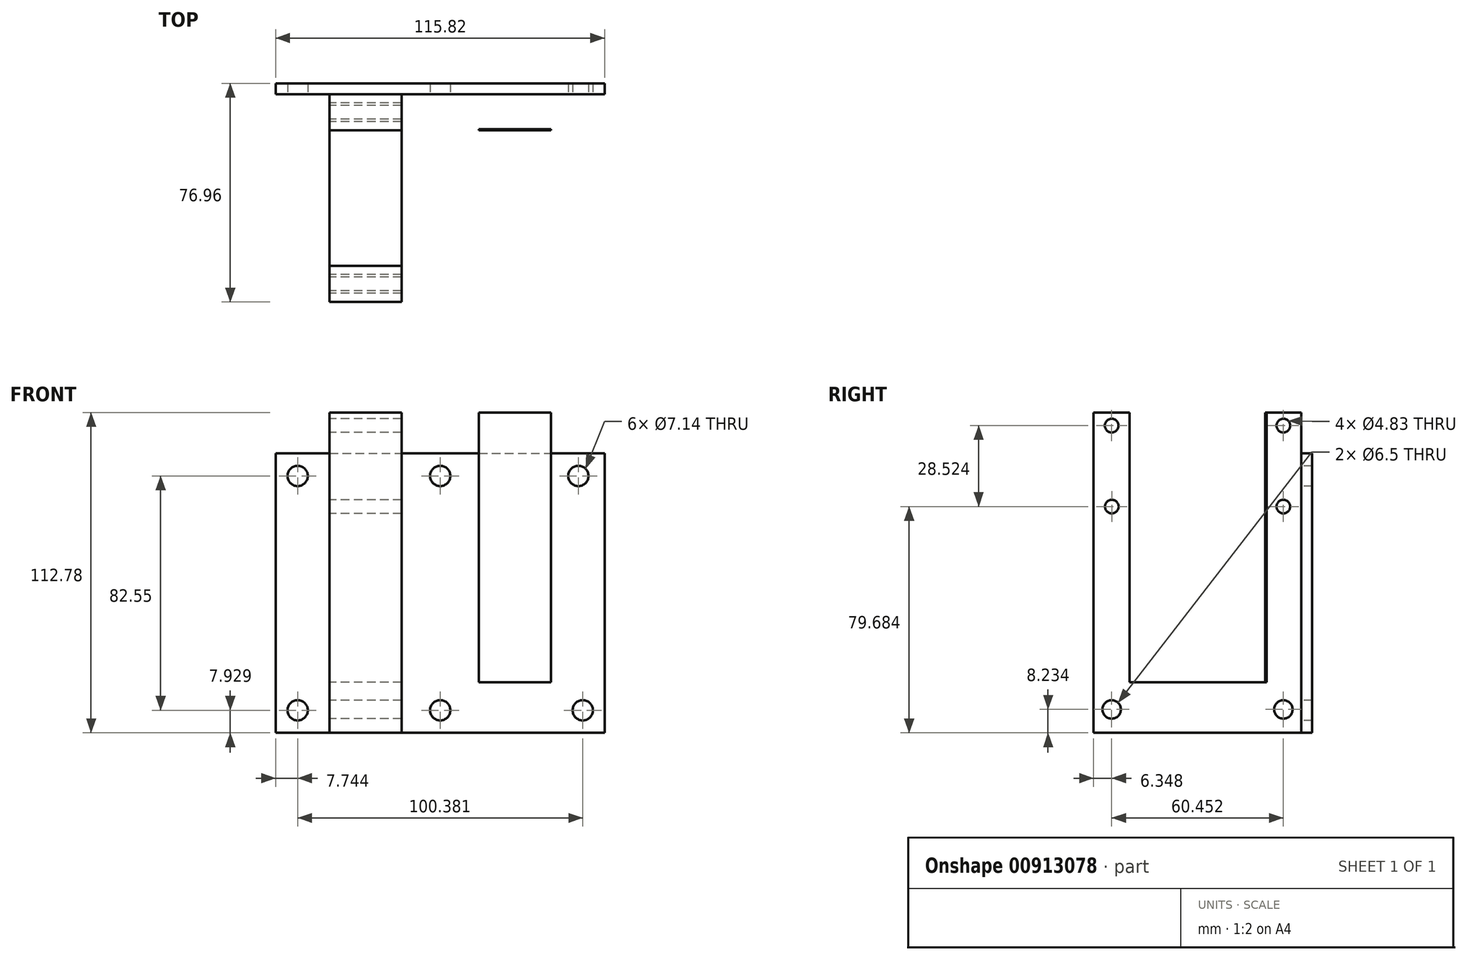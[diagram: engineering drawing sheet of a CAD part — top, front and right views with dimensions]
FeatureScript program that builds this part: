
annotation { "Feature Type Name" : "Feature", "Feature Type Description" : "" }
export const myFeature = defineFeature(function(context is Context, id is Id, definition is map)
    precondition{}
    {
        {
            var Q0;
            Q0=qCreatedBy(makeId("Front.planeOp"),FACE);
            var sketch = newSketch(context, id + "F0", { "sketchPlane" : qUnion([Q0])});
            skLineSegment(sketch, "E0", {"start": v(-55.41, 38.66) * mm, "end": v(60.41, 38.66) * mm});
            skLineSegment(sketch, "E1", {"start": v(60.41, 38.66) * mm, "end": v(60.41, -59.74) * mm});
            skLineSegment(sketch, "E2", {"start": v(60.41, -59.74) * mm, "end": v(-55.41, -59.74) * mm});
            skLineSegment(sketch, "E3", {"start": v(-55.41, 38.66) * mm, "end": v(-55.41, -59.74) * mm});
            skCircle(sketch, "E4", {"center": v(-47.67, -51.81) * mm, "radius": 3.57 * mm});
            skCircle(sketch, "E5", {"center": v(2.52, -51.81) * mm, "radius": 3.57 * mm});
            skCircle(sketch, "E6", {"center": v(52.71, -51.81) * mm, "radius": 3.57 * mm});
            skCircle(sketch, "E7", {"center": v(-47.67, 30.74) * mm, "radius": 3.57 * mm});
            skCircle(sketch, "E8", {"center": v(2.52, 30.74) * mm, "radius": 3.57 * mm});
            skCircle(sketch, "E9", {"center": v(51.17, 30.74) * mm, "radius": 3.57 * mm});
            skLineSegment(sketch, "E10.bottom", {"start": v(-36.46, -59.74) * mm, "end": v(-11.06, -59.74) * mm});
            skLineSegment(sketch, "E10.top", {"start": v(-36.46, 53.04) * mm, "end": v(-11.06, 53.04) * mm});
            skLineSegment(sketch, "E10.left", {"start": v(-36.46, -59.74) * mm, "end": v(-36.46, 53.04) * mm});
            skLineSegment(sketch, "E10.right", {"start": v(-11.06, -59.74) * mm, "end": v(-11.06, 53.04) * mm});
            skLineSegment(sketch, "E11.bottom", {"start": v(16.11, -59.74) * mm, "end": v(41.51, -59.74) * mm});
            skLineSegment(sketch, "E11.top", {"start": v(16.11, 53.04) * mm, "end": v(41.51, 53.04) * mm});
            skLineSegment(sketch, "E11.left", {"start": v(16.11, -59.74) * mm, "end": v(16.11, 53.04) * mm});
            skLineSegment(sketch, "E11.right", {"start": v(41.51, -59.74) * mm, "end": v(41.51, 53.04) * mm});
            skSolve(sketch);
        }
        {
            var Q0;
            {var subQ5=sQuery(id+"F0.wireOp",EDGE,"E10.top");Q0=makeQuery(id+"F0.imprint","IMPRINT",FACE,{"disambiguationData":[TD([[makeQuery(id+"F0.imprint","IMPRINT",EDGE,{"derivedFrom":subQ5}),-1.0]])]});}
            var Q1;
            {var subQ0=sQuery(id+"F0.wireOp",EDGE,"E10.right");var subQ1=sQuery(id+"F0.wireOp",EDGE,"E0");var subQ2=makeQuery(id+"F0.imprint","INTERSECT",VERTEX,{"derivedFrom":[subQ1,subQ0]});Q1=makeQuery(id+"F0.imprint","IMPRINT",FACE,{"disambiguationData":[TD([[makeQuery(id+"F0.imprint","IMPRINT",EDGE,{"disambiguationData":[TD([[subQ2,1.0]])],"derivedFrom":subQ1}),-1.0]])]});}
            var Q2;
            {var subQ0=sQuery(id+"F0.wireOp",EDGE,"E11.left");var subQ1=sQuery(id+"F0.wireOp",EDGE,"E0");var subQ2=makeQuery(id+"F0.imprint","INTERSECT",VERTEX,{"derivedFrom":[subQ1,subQ0]});Q2=makeQuery(id+"F0.imprint","IMPRINT",FACE,{"disambiguationData":[TD([[makeQuery(id+"F0.imprint","IMPRINT",EDGE,{"disambiguationData":[TD([[subQ2,-1.0]])],"derivedFrom":subQ1}),-1.0]])]});}
            var Q3;
            {var subQ5=sQuery(id+"F0.wireOp",EDGE,"E11.top");Q3=makeQuery(id+"F0.imprint","IMPRINT",FACE,{"disambiguationData":[TD([[makeQuery(id+"F0.imprint","IMPRINT",EDGE,{"derivedFrom":subQ5}),-1.0]])]});}
            extrude(context, id + "F1", {"entities" : qUnion([Q0, Q1, Q2, Q3]), "depth" : 73.15 * mm, "offsetDistance" : 25.4 * mm});
        }
        {
            var Q0;
            Q0=makeQuery(id+"F0.imprint","IMPRINT",FACE,{"disambiguationData":[TD([[makeQuery(id+"F0.imprint","IMPRINT",EDGE,{"derivedFrom":sQuery(id+"F0.wireOp",EDGE,"E5")}),-1.0]])]});
            var Q1;
            {var subQ1=sQuery(id+"F0.wireOp",EDGE,"E1");Q1=makeQuery(id+"F0.imprint","IMPRINT",FACE,{"disambiguationData":[TD([[makeQuery(id+"F0.imprint","IMPRINT",EDGE,{"derivedFrom":subQ1}),-1.0]])]});}
            var Q2;
            {var subQ0=sQuery(id+"F0.wireOp",EDGE,"E11.left");var subQ1=sQuery(id+"F0.wireOp",EDGE,"E0");var subQ2=makeQuery(id+"F0.imprint","INTERSECT",VERTEX,{"derivedFrom":[subQ1,subQ0]});Q2=makeQuery(id+"F0.imprint","IMPRINT",FACE,{"disambiguationData":[TD([[makeQuery(id+"F0.imprint","IMPRINT",EDGE,{"disambiguationData":[TD([[subQ2,-1.0]])],"derivedFrom":subQ1}),-1.0]])]});}
            var Q3;
            {var subQ0=sQuery(id+"F0.wireOp",EDGE,"E10.right");var subQ1=sQuery(id+"F0.wireOp",EDGE,"E0");var subQ2=makeQuery(id+"F0.imprint","INTERSECT",VERTEX,{"derivedFrom":[subQ1,subQ0]});Q3=makeQuery(id+"F0.imprint","IMPRINT",FACE,{"disambiguationData":[TD([[makeQuery(id+"F0.imprint","IMPRINT",EDGE,{"disambiguationData":[TD([[subQ2,1.0]])],"derivedFrom":subQ1}),-1.0]])]});}
            var Q4;
            {var subQ0=sQuery(id+"F0.wireOp",EDGE,"E3");Q4=makeQuery(id+"F0.imprint","IMPRINT",FACE,{"disambiguationData":[TD([[makeQuery(id+"F0.imprint","IMPRINT",EDGE,{"derivedFrom":subQ0}),1.0]])]});}
            extrude(context, id + "F2", {"entities" : qUnion([Q0, Q1, Q2, Q3, Q4]), "oppositeDirection" : true, "depth" : 3.8 * mm, "offsetDistance" : 25.4 * mm});
        }
        {
            var Q0;
            Q0=makeQuery(id+"F1.opExtrude","SWEPT_FACE",FACE,{"disambiguationData":[OSD([sQuery(id+"F0.wireOp",EDGE,"E10.left")])]});
            var sketch = newSketch(context, id + "F3", { "sketchPlane" : qUnion([Q0])});
            skLineSegment(sketch, "E12", {"start": v(12.7, 53.04) * mm, "end": v(12.7, -41.96) * mm});
            skLineSegment(sketch, "E13", {"start": v(12.7, -41.96) * mm, "end": v(60.45, -41.96) * mm});
            skLineSegment(sketch, "E14", {"start": v(60.45, 53.04) * mm, "end": v(60.45, -41.96) * mm});
            skLineSegment(sketch, "E15", {"start": v(60.45, 53.04) * mm, "end": v(12.7, 53.04) * mm});
            skLineSegment(sketch, "E16", {"start": v(12.7, 53.04) * mm, "end": v(60.45, 53.04) * mm});
            skCircle(sketch, "E17", {"center": v(6.35, 48.47) * mm, "radius": 2.41 * mm});
            skCircle(sketch, "E18", {"center": v(66.8, 48.47) * mm, "radius": 2.41 * mm});
            skCircle(sketch, "E19", {"center": v(6.35, 19.94) * mm, "radius": 2.41 * mm});
            skCircle(sketch, "E20", {"center": v(66.75, 19.94) * mm, "radius": 2.41 * mm});
            skCircle(sketch, "E21", {"center": v(6.35, -51.5) * mm, "radius": 3.25 * mm});
            skCircle(sketch, "E22", {"center": v(66.8, -51.5) * mm, "radius": 3.25 * mm});
            skSolve(sketch);
        }
        {
            var Q0;
            Q0=makeQuery(id+"F3.imprint","IMPRINT",FACE,{"disambiguationData":[TD([[makeQuery(id+"F3.imprint","IMPRINT",EDGE,{"derivedFrom":sQuery(id+"F3.wireOp",EDGE,"E12")}),1.0]])]});
            var Q1;
            Q1=makeQuery(id+"F3.imprint","IMPRINT",FACE,{"disambiguationData":[TD([[makeQuery(id+"F3.imprint","IMPRINT",EDGE,{"derivedFrom":sQuery(id+"F3.wireOp",EDGE,"E19")}),1.0]])]});
            var Q2;
            Q2=makeQuery(id+"F3.imprint","IMPRINT",FACE,{"disambiguationData":[TD([[makeQuery(id+"F3.imprint","IMPRINT",EDGE,{"derivedFrom":sQuery(id+"F3.wireOp",EDGE,"E20")}),1.0]])]});
            var Q3;
            Q3=makeQuery(id+"F3.imprint","IMPRINT",FACE,{"disambiguationData":[TD([[makeQuery(id+"F3.imprint","IMPRINT",EDGE,{"derivedFrom":sQuery(id+"F3.wireOp",EDGE,"E18")}),1.0]])]});
            var Q4;
            Q4=makeQuery(id+"F3.imprint","IMPRINT",FACE,{"disambiguationData":[TD([[makeQuery(id+"F3.imprint","IMPRINT",EDGE,{"derivedFrom":sQuery(id+"F3.wireOp",EDGE,"E17")}),1.0]])]});
            var Q5;
            Q5=makeQuery(id+"F3.imprint","IMPRINT",FACE,{"disambiguationData":[TD([[makeQuery(id+"F3.imprint","IMPRINT",EDGE,{"derivedFrom":sQuery(id+"F3.wireOp",EDGE,"E21")}),1.0]])]});
            var Q6;
            Q6=makeQuery(id+"F3.imprint","IMPRINT",FACE,{"disambiguationData":[TD([[makeQuery(id+"F3.imprint","IMPRINT",EDGE,{"derivedFrom":sQuery(id+"F3.wireOp",EDGE,"E22")}),1.0]])]});
            extrude(context, id + "F4", {"entities" : qUnion([Q0, Q1, Q2, Q3, Q4, Q5, Q6]), "operationType" : NewBodyOperationType.REMOVE, "endBound" : BoundingType.THROUGH_ALL, "oppositeDirection" : true, "depth" : 50.8 * mm, "offsetDistance" : 25.4 * mm});
        }
        {
            var Q0;
            Q0=makeQuery(id+"F1.opExtrude","SWEPT_FACE",FACE,{"disambiguationData":[OSD([sQuery(id+"F0.wireOp",EDGE,"E11.right")])]});
            var sketch = newSketch(context, id + "F5", { "sketchPlane" : qUnion([Q0])});
            skLineSegment(sketch, "E23", {"start": v(-60, 53.04) * mm, "end": v(-60, -41.96) * mm});
            skLineSegment(sketch, "E24", {"start": v(-60, -41.96) * mm, "end": v(-12.26, -41.96) * mm});
            skLineSegment(sketch, "E25", {"start": v(-12.26, -41.96) * mm, "end": v(-12.26, 53.04) * mm});
            skLineSegment(sketch, "E26", {"start": v(-12.26, 53.04) * mm, "end": v(-60, 53.04) * mm});
            skCircle(sketch, "E27", {"center": v(-66.8, 48.47) * mm, "radius": 2.41 * mm});
            skCircle(sketch, "E28", {"center": v(-6.35, 48.47) * mm, "radius": 2.41 * mm});
            skCircle(sketch, "E29", {"center": v(-66.8, 19.94) * mm, "radius": 2.41 * mm});
            skCircle(sketch, "E30", {"center": v(-6.35, 19.94) * mm, "radius": 2.41 * mm});
            skCircle(sketch, "E31", {"center": v(-66.8, -51.5) * mm, "radius": 3.25 * mm});
            skCircle(sketch, "E32", {"center": v(-6.35, -51.5) * mm, "radius": 3.25 * mm});
            skSolve(sketch);
        }
        {
            var Q0;
            Q0=makeQuery(id+"F5.imprint","IMPRINT",FACE,{"disambiguationData":[TD([[makeQuery(id+"F5.imprint","IMPRINT",EDGE,{"derivedFrom":sQuery(id+"F5.wireOp",EDGE,"E27")}),1.0]])]});
            var Q1;
            Q1=makeQuery(id+"F5.imprint","IMPRINT",FACE,{"disambiguationData":[TD([[makeQuery(id+"F5.imprint","IMPRINT",EDGE,{"derivedFrom":sQuery(id+"F5.wireOp",EDGE,"E29")}),1.0]])]});
            var Q2;
            Q2=makeQuery(id+"F5.imprint","IMPRINT",FACE,{"disambiguationData":[TD([[makeQuery(id+"F5.imprint","IMPRINT",EDGE,{"derivedFrom":sQuery(id+"F5.wireOp",EDGE,"E31")}),1.0]])]});
            var Q3;
            Q3=makeQuery(id+"F5.imprint","IMPRINT",FACE,{"disambiguationData":[TD([[makeQuery(id+"F5.imprint","IMPRINT",EDGE,{"derivedFrom":sQuery(id+"F5.wireOp",EDGE,"E32")}),1.0]])]});
            var Q4;
            Q4=makeQuery(id+"F5.imprint","IMPRINT",FACE,{"disambiguationData":[TD([[makeQuery(id+"F5.imprint","IMPRINT",EDGE,{"derivedFrom":sQuery(id+"F5.wireOp",EDGE,"E30")}),1.0]])]});
            var Q5;
            Q5=makeQuery(id+"F5.imprint","IMPRINT",FACE,{"disambiguationData":[TD([[makeQuery(id+"F5.imprint","IMPRINT",EDGE,{"derivedFrom":sQuery(id+"F5.wireOp",EDGE,"E28")}),1.0]])]});
            var Q6;
            Q6=makeQuery(id+"F5.imprint","IMPRINT",FACE,{"disambiguationData":[TD([[makeQuery(id+"F5.imprint","IMPRINT",EDGE,{"derivedFrom":sQuery(id+"F5.wireOp",EDGE,"E23")}),1.0]])]});
            extrude(context, id + "F6", {"entities" : qUnion([Q0, Q1, Q2, Q3, Q4, Q5, Q6]), "operationType" : NewBodyOperationType.REMOVE, "oppositeDirection" : true, "depth" : 25.4 * mm, "offsetDistance" : 25.4 * mm});
        }
    });
